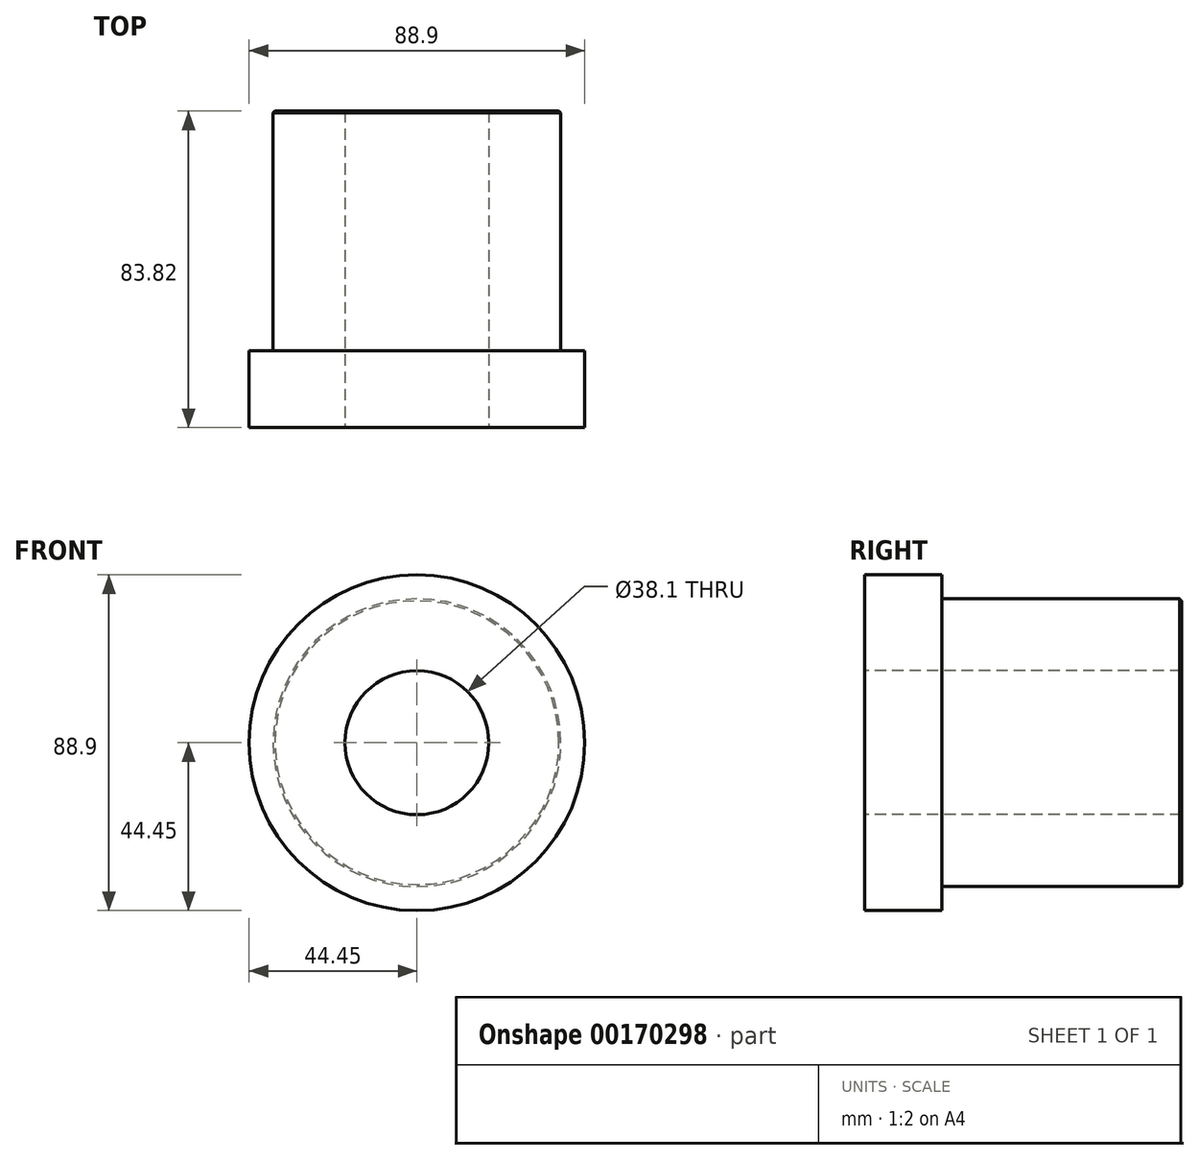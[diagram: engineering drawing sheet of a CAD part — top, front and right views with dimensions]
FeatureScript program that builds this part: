
annotation { "Feature Type Name" : "Feature", "Feature Type Description" : "" }
export const myFeature = defineFeature(function(context is Context, id is Id, definition is map)
    precondition{}
    {
        {
            var Q0;
            Q0=qCreatedBy(makeId("Front.planeOp"),FACE);
            var sketch = newSketch(context, id + "F0", { "sketchPlane" : qUnion([Q0])});
            skCircle(sketch, "E0", {"center": v(0, 0) * mm, "radius": 44.45 * mm});
            skSolve(sketch);
        }
        {
            var Q0;
            Q0=makeQuery(id+"F0.imprint","IMPRINT",FACE,{"disambiguationData":[TD([[makeQuery(id+"F0.imprint","IMPRINT",EDGE,{"derivedFrom":sQuery(id+"F0.wireOp",EDGE,"E0")}),1.0]])]});
            extrude(context, id + "F1", {"entities" : qUnion([Q0]), "depth" : 20.32 * mm});
        }
        {
            var Q0;
            Q0=makeQuery(id+"F1.opExtrude","CAP_FACE",FACE,{"disambiguationData":[OSD([sQuery(id+"F0.wireOp",EDGE,"E0")])],"isStart":true});
            var sketch = newSketch(context, id + "F2", { "sketchPlane" : qUnion([Q0])});
            skCircle(sketch, "E1", {"center": v(0, 0) * mm, "radius": 38.1 * mm});
            skSolve(sketch);
        }
        {
            var Q0;
            Q0=makeQuery(id+"F2.imprint","IMPRINT",FACE,{"disambiguationData":[TD([[makeQuery(id+"F2.imprint","IMPRINT",EDGE,{"derivedFrom":sQuery(id+"F2.wireOp",EDGE,"E1")}),1.0]])]});
            extrude(context, id + "F3", {"entities" : qUnion([Q0]), "operationType" : NewBodyOperationType.ADD, "depth" : 63.5 * mm});
        }
        {
            var Q0;
            Q0=makeQuery(id+"F3.opExtrude","CAP_EDGE",EDGE,{"disambiguationData":[OSD([sQuery(id+"F2.wireOp",EDGE,"E1")])],"isStart":false});
            chamfer(context, id + "F4", {"entities" : qUnion([Q0]), "width" : 0.5 * mm, "tangentPropagation" : true});
        }
        {
            var Q0;
            Q0=makeQuery(id+"F1.opExtrude","CAP_FACE",FACE,{"disambiguationData":[OSD([sQuery(id+"F0.wireOp",EDGE,"E0")])],"isStart":false});
            var sketch = newSketch(context, id + "F5", { "sketchPlane" : qUnion([Q0])});
            skCircle(sketch, "E2", {"center": v(0, 0) * mm, "radius": 19.05 * mm});
            skSolve(sketch);
        }
        {
            var Q0;
            Q0=sQuery(id+"F5.wireOp",VERTEX,"E2.center");
            var Q1;
            Q1=makeQuery(id+"F1.opExtrude","SWEPT_BODY",BODY,{"disambiguationData":[OSD([sQuery(id+"F0.wireOp",EDGE,"E0")])]});
            hole(context, id + "F6", {"style" : HoleStyle.SIMPLE, "endStyle" : HoleEndStyle.THROUGH, "holeDiameter" : 38.1 * mm, "locations" : qUnion([Q0]), "scope" : qUnion([Q1]), "isTappedThrough" : true});
        }
    });
